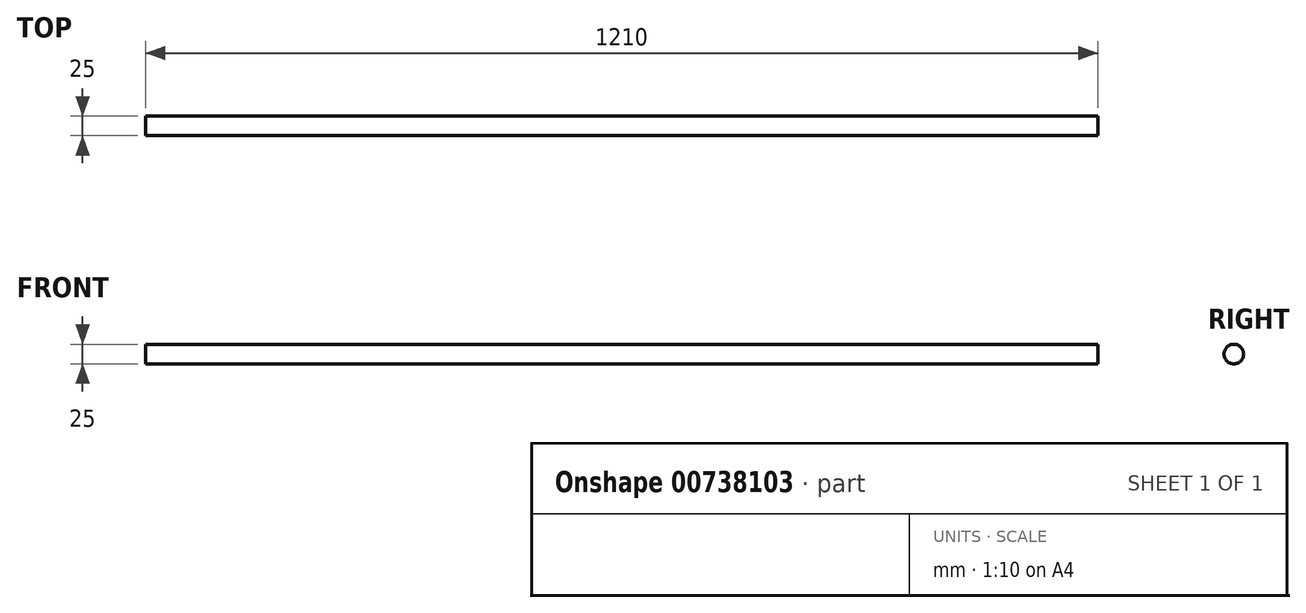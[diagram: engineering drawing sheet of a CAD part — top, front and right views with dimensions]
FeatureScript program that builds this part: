
annotation { "Feature Type Name" : "Feature", "Feature Type Description" : "" }
export const myFeature = defineFeature(function(context is Context, id is Id, definition is map)
    precondition{}
    {
        {
            var Q0;
            Q0=qCreatedBy(makeId("Right.planeOp"),FACE);
            var sketch = newSketch(context, id + "F0", { "sketchPlane" : qUnion([Q0])});
            skCircle(sketch, "E0", {"center": v(0.07, 0.27) * mm, "radius": 12.5 * mm});
            skSolve(sketch);
        }
        {
            var Q0;
            Q0 = qSketchRegion(id + "F0", true);
            extrude(context, id + "F1", {"entities" : qUnion([Q0]), "depth" : 1210 * mm, "offsetDistance" : 25 * mm});
        }
    });
